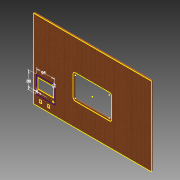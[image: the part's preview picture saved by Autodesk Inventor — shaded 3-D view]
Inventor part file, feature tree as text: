
AUTODESK INVENTOR PART (.ipt)
format: ipt  version: 2015 SP1 (Build 190203100, 203)  size: 799,232 bytes
history: native  units: in
note: dims shown in document units (in); Inventor stores cm internally (conversion verified against a paired STEP export)
features: reference x13, sketch x5, extrude x4, projected_geometry x2
ambient origin geometry x8: Origin, YZ Plane, XZ Plane, XY Plane, X Axis, Y Axis, Z Axis, Center Point
bodies: Solid1 (feature_tree)
feature tree (24):
  extrude  "Extrusion1"  Depth=0.1575in TaperAngle=0.0deg
  extrude  "Extrusion2"  Depth=0.7874in
  extrude  "Extrusion3"  Depth=0.4331in
  sketch  "Sketch5"  dims[d8=1.1811in d9=0.4331in]
  extrude  "Extrusion4"  Depth=0.4331in
  sketch  "Sketch2"  dims[d0=0.315in d1=0.0in d2=0.1575in d3=0.0in]
  reference  "Reference3"
  reference  "Reference4"
  reference  "Reference5"
  reference  "Reference6"
  reference  "Reference7"
  sketch  "Sketch3"  dims[d4=1.1811in d5=0.7874in]
  reference  "Reference8"
  reference  "Reference9"
  reference  "Reference10"
  reference  "Reference11"
  reference  "Reference12"
  reference  "Reference13"
  reference  "Reference14"
  reference  "Reference15"
  sketch  "Sketch4"  dims[d6=0.5512in d7=0.4331in]
  sketch  "Sketch6"  dims[d10=0.5906in d11=0.5906in d12=1.063in d13=2.0079in d14=0.315in d15=3.7008in d16=3.1102in d17=0.315in d19=3.3465in d20=0.3543in d21=0.1575in d22=0.0in d23=3.4646in d24=3.7008in d25=0.315in d26=0.3937in d27=3.7008in d28=3.4646in d29=0.315in d30=0.3937in d31=0.1378in d32=0.0in]
  projected_geometry  "Project Cut Edges1"
  projected_geometry  "Project Cut Edges2"
